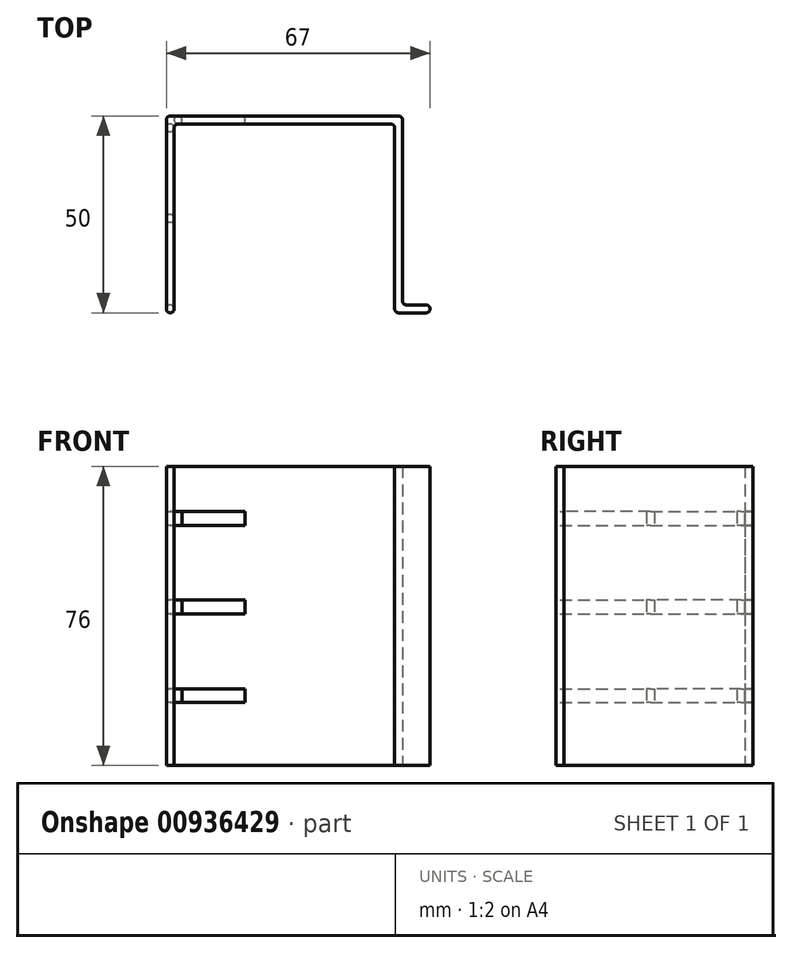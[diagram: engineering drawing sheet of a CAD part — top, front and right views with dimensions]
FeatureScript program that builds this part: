
annotation { "Feature Type Name" : "Feature", "Feature Type Description" : "" }
export const myFeature = defineFeature(function(context is Context, id is Id, definition is map)
    precondition{}
    {
        {
            var Q0;
            Q0=qCreatedBy(makeId("Top.planeOp"),FACE);
            var sketch = newSketch(context, id + "F0", { "sketchPlane" : qUnion([Q0])});
            skLineSegment(sketch, "E0", {"start": v(0, 1) * mm, "end": v(0, 47) * mm});
            skLineSegment(sketch, "E1", {"start": v(1, 48) * mm, "end": v(55, 48) * mm});
            skLineSegment(sketch, "E2", {"start": v(56, 47) * mm, "end": v(56, 1) * mm});
            skLineSegment(sketch, "E3", {"start": v(57, 0) * mm, "end": v(64, 0) * mm});
            skLineSegment(sketch, "E4.0", {"start": v(59, 2) * mm, "end": v(64, 2) * mm});
            skLineSegment(sketch, "E4.1", {"start": v(58, 49) * mm, "end": v(58, 3) * mm});
            skLineSegment(sketch, "E4.2", {"start": v(-1, 50) * mm, "end": v(57, 50) * mm});
            skLineSegment(sketch, "E4.3", {"start": v(-2, 1) * mm, "end": v(-2, 49) * mm});
            skLineSegment(sketch, "E5", {"start": v(65, 1) * mm, "end": v(65, 1) * mm});
            skLineSegment(sketch, "E6", {"start": v(-1, 0) * mm, "end": v(-1, 0) * mm});
            skPoint(sketch, "E7.visualSharp", {"position": v(0, 48) * mm});
            skArc(sketch, "E7.filletArc", {"start": v(1, 48) * mm, "mid": v(0.3, 47.7) * mm, "end": v(0, 47) * mm});
            skPoint(sketch, "E8.visualSharp", {"position": v(-2, 50) * mm});
            skArc(sketch, "E8.filletArc", {"start": v(-1, 50) * mm, "mid": v(-1.7, 49.7) * mm, "end": v(-2, 49) * mm});
            skPoint(sketch, "E9.visualSharp", {"position": v(58, 50) * mm});
            skArc(sketch, "E9.filletArc", {"start": v(58, 49) * mm, "mid": v(57.7, 49.7) * mm, "end": v(57, 50) * mm});
            skPoint(sketch, "E10.visualSharp", {"position": v(56, 48) * mm});
            skArc(sketch, "E10.filletArc", {"start": v(56, 47) * mm, "mid": v(55.7, 47.7) * mm, "end": v(55, 48) * mm});
            skPoint(sketch, "E11.visualSharp", {"position": v(58, 2) * mm});
            skArc(sketch, "E11.filletArc", {"start": v(58, 3) * mm, "mid": v(58.3, 2.3) * mm, "end": v(59, 2) * mm});
            skPoint(sketch, "E12.visualSharp", {"position": v(56, 0) * mm});
            skArc(sketch, "E12.filletArc", {"start": v(56, 1) * mm, "mid": v(56.3, 0.3) * mm, "end": v(57, 0) * mm});
            skPoint(sketch, "E13.visualSharp", {"position": v(65, 2) * mm});
            skArc(sketch, "E13.filletArc", {"start": v(65, 1) * mm, "mid": v(64.7, 1.7) * mm, "end": v(64, 2) * mm});
            skPoint(sketch, "E14.visualSharp", {"position": v(65, 0) * mm});
            skArc(sketch, "E14.filletArc", {"start": v(64, 0) * mm, "mid": v(64.7, 0.3) * mm, "end": v(65, 1) * mm});
            skPoint(sketch, "E15.visualSharp", {"position": v(-2, 0) * mm});
            skArc(sketch, "E15.filletArc", {"start": v(-2, 1) * mm, "mid": v(-1.7, 0.3) * mm, "end": v(-1, 0) * mm});
            skPoint(sketch, "E16.visualSharp", {"position": v(0, 0) * mm});
            skArc(sketch, "E16.filletArc", {"start": v(-1, 0) * mm, "mid": v(-0.3, 0.3) * mm, "end": v(0, 1) * mm});
            skSolve(sketch);
        }
        {
            var Q0;
            Q0=makeQuery(id+"F0.imprint","IMPRINT",FACE,{"disambiguationData":[TD([[makeQuery(id+"F0.imprint","IMPRINT",EDGE,{"derivedFrom":sQuery(id+"F0.wireOp",EDGE,"E0")}),1.0]])]});
            extrude(context, id + "F1", {"entities" : qUnion([Q0]), "depth" : 76 * mm, "offsetDistance" : 25 * mm});
        }
        {
            var Q0;
            Q0=makeQuery(id+"F1.opExtrude","SWEPT_FACE",FACE,{"disambiguationData":[OSD([sQuery(id+"F0.wireOp",EDGE,"E4.2")])]});
            var sketch = newSketch(context, id + "F2", { "sketchPlane" : qUnion([Q0])});
            skLineSegment(sketch, "E17", {"start": v(2, 16) * mm, "end": v(-18, 16) * mm});
            skLineSegment(sketch, "E18", {"start": v(-18, 16) * mm, "end": v(-18, 19.5) * mm});
            skLineSegment(sketch, "E19", {"start": v(-18, 19.5) * mm, "end": v(2, 19.5) * mm});
            skLineSegment(sketch, "E20.0", {"start": v(2, 76) * mm, "end": v(2, 0) * mm});
            skLineSegment(sketch, "E21", {"start": v(2, 19.5) * mm, "end": v(2, 16) * mm});
            skLineSegment(sketch, "E22.0.1.0", {"start": v(-18, 42) * mm, "end": v(2, 42) * mm});
            skLineSegment(sketch, "E22.0.1.1", {"start": v(2, 42) * mm, "end": v(2, 38.5) * mm});
            skLineSegment(sketch, "E22.0.1.2", {"start": v(2, 38.5) * mm, "end": v(-18, 38.5) * mm});
            skLineSegment(sketch, "E22.0.1.3", {"start": v(-18, 38.5) * mm, "end": v(-18, 42) * mm});
            skLineSegment(sketch, "E22.0.2.0", {"start": v(-18, 64.5) * mm, "end": v(2, 64.5) * mm});
            skLineSegment(sketch, "E22.0.2.1", {"start": v(2, 64.5) * mm, "end": v(2, 61) * mm});
            skLineSegment(sketch, "E22.0.2.2", {"start": v(2, 61) * mm, "end": v(-18, 61) * mm});
            skLineSegment(sketch, "E22.0.2.3", {"start": v(-18, 61) * mm, "end": v(-18, 64.5) * mm});
            skLineSegment(sketch, "E22.direction1", {"start": v(-18, 16) * mm, "end": v(7, 16) * mm, "construction": true});
            skLineSegment(sketch, "E22.direction2", {"start": v(-18, 16) * mm, "end": v(-18, 38.5) * mm, "construction": true});
            skSolve(sketch);
        }
        {
            var Q0;
            {var subQ0=sQuery(id+"F2.wireOp",EDGE,"E18");var subQ1=sQuery(id+"F2.wireOp",EDGE,"E17");var subQ7=sQuery(id+"F2.wireOp",EDGE,"E20.0");var subQ8=makeQuery(id+"F2.imprint","INTERSECT",VERTEX,{"derivedFrom":[subQ1,subQ7]});Q0=qUnion([makeQuery(id+"F2.imprint","IMPRINT",FACE,{"disambiguationData":[TD([[makeQuery(id+"F2.imprint","IMPRINT",EDGE,{"disambiguationData":[TD([[subQ8,1.0]])],"derivedFrom":subQ7}),-1.0]])]}),makeQuery(id+"F2.imprint","IMPRINT",FACE,{"disambiguationData":[TD([[makeQuery(id+"F2.imprint","IMPRINT",EDGE,{"derivedFrom":subQ0}),-1.0]])]})]);}
            var Q1;
            Q1=makeQuery(id+"F2.imprint","IMPRINT",FACE,{"disambiguationData":[TD([[makeQuery(id+"F2.imprint","IMPRINT",EDGE,{"derivedFrom":sQuery(id+"F2.wireOp",EDGE,"e2ad7010-09eb-4918-bae3-de0be9d5e85c.0.1.0")}),-1.0]])]});
            var Q2;
            Q2=makeQuery(id+"F2.imprint","IMPRINT",FACE,{"disambiguationData":[TD([[makeQuery(id+"F2.imprint","IMPRINT",EDGE,{"derivedFrom":sQuery(id+"F2.wireOp",EDGE,"e2ad7010-09eb-4918-bae3-de0be9d5e85c.0.2.0")}),-1.0]])]});
            var Q3;
            {var subQ0=sQuery(id+"F2.wireOp",EDGE,"E22.0.1.3");Q3=makeQuery(id+"F2.imprint","IMPRINT",FACE,{"disambiguationData":[TD([[makeQuery(id+"F2.imprint","IMPRINT",EDGE,{"derivedFrom":subQ0}),-1.0]])]});}
            var Q4;
            {var subQ0=sQuery(id+"F2.wireOp",EDGE,"E22.0.2.3");Q4=makeQuery(id+"F2.imprint","IMPRINT",FACE,{"disambiguationData":[TD([[makeQuery(id+"F2.imprint","IMPRINT",EDGE,{"derivedFrom":subQ0}),-1.0]])]});}
            var Q5;
            {var subQ0=sQuery(id+"F2.wireOp",EDGE,"E22.0.1.0");var subQ1=sQuery(id+"F2.wireOp",EDGE,"E20.0");var subQ2=makeQuery(id+"F2.imprint","INTERSECT",VERTEX,{"derivedFrom":[subQ1,subQ0]});Q5=makeQuery(id+"F2.imprint","IMPRINT",FACE,{"disambiguationData":[TD([[makeQuery(id+"F2.imprint","IMPRINT",EDGE,{"disambiguationData":[TD([[subQ2,-1.0]])],"derivedFrom":subQ1}),-1.0]])]});}
            var Q6;
            {var subQ0=sQuery(id+"F2.wireOp",EDGE,"E22.0.2.2");var subQ1=sQuery(id+"F2.wireOp",EDGE,"E20.0");var subQ2=makeQuery(id+"F2.imprint","INTERSECT",VERTEX,{"derivedFrom":[subQ1,subQ0]});Q6=makeQuery(id+"F2.imprint","IMPRINT",FACE,{"disambiguationData":[TD([[makeQuery(id+"F2.imprint","IMPRINT",EDGE,{"disambiguationData":[TD([[subQ2,1.0]])],"derivedFrom":subQ1}),-1.0]])]});}
            extrude(context, id + "F3", {"entities" : qUnion([Q0, Q1, Q2, Q3, Q4, Q5, Q6]), "operationType" : NewBodyOperationType.REMOVE, "endBound" : BoundingType.THROUGH_ALL, "oppositeDirection" : true, "depth" : 25 * mm, "offsetDistance" : 25 * mm});
        }
        {
            var Q0;
            Q0=makeQuery(id+"F3.boolean.opBoolean","COPY",FACE,{"derivedFrom":makeQuery(id+"F3.opExtrude","SWEPT_FACE",FACE,{"disambiguationData":[OSD([sQuery(id+"F2.wireOp",EDGE,"E17")])]})});
            var sketch = newSketch(context, id + "F4", { "sketchPlane" : qUnion([Q0])});
            skLineSegment(sketch, "E23.0", {"start": v(-2, 1) * mm, "end": v(-2, 49) * mm});
            skPoint(sketch, "E24.0", {"position": v(-1.7, 49.7) * mm});
            skLineSegment(sketch, "E25.0", {"start": v(-1, 50) * mm, "end": v(18, 50) * mm});
            skLineSegment(sketch, "E26.0", {"start": v(1, 48) * mm, "end": v(18, 48) * mm});
            skArc(sketch, "E27.0", {"start": v(1, 48) * mm, "mid": v(0.3, 47.7) * mm, "end": v(0, 47) * mm});
            skLineSegment(sketch, "E28.0", {"start": v(0, 1) * mm, "end": v(0, 47) * mm});
            skLineSegment(sketch, "E29.0", {"start": v(18, 48) * mm, "end": v(18, 50) * mm});
            skArc(sketch, "E30.0", {"start": v(-2, 1) * mm, "mid": v(-1, 0) * mm, "end": v(0, 1) * mm});
            skArc(sketch, "E31.0", {"start": v(-1, 50) * mm, "mid": v(-1.7, 49.7) * mm, "end": v(-2, 49) * mm});
            skCircle(sketch, "E32", {"center": v(-1, 1) * mm, "radius": 1 * mm});
            skCircle(sketch, "E33", {"center": v(-1, 47) * mm, "radius": 1 * mm});
            skCircle(sketch, "E34", {"center": v(-1, 24) * mm, "radius": 1 * mm});
            skLineSegment(sketch, "E35", {"start": v(0, 47) * mm, "end": v(-2, 47) * mm, "construction": true});
            skLineSegment(sketch, "E36", {"start": v(-1, 47) * mm, "end": v(-1, 1) * mm, "construction": true});
            skLineSegment(sketch, "E37", {"start": v(1, 48) * mm, "end": v(1, 50) * mm, "construction": true});
            skCircle(sketch, "E38", {"center": v(1, 49) * mm, "radius": 1 * mm});
            skSolve(sketch);
        }
        {
            var Q0;
            Q0=makeQuery(id+"F4.imprint","IMPRINT",FACE,{"disambiguationData":[TD([[makeQuery(id+"F4.imprint","IMPRINT",EDGE,{"derivedFrom":sQuery(id+"F4.wireOp",EDGE,"E33")}),1.0]])]});
            var Q1;
            Q1=makeQuery(id+"F4.imprint","IMPRINT",FACE,{"disambiguationData":[TD([[makeQuery(id+"F4.imprint","IMPRINT",EDGE,{"derivedFrom":sQuery(id+"F4.wireOp",EDGE,"E34")}),1.0]])]});
            var Q2;
            Q2=makeQuery(id+"F4.imprint","IMPRINT",FACE,{"disambiguationData":[TD([[makeQuery(id+"F4.imprint","IMPRINT",EDGE,{"derivedFrom":sQuery(id+"F4.wireOp",EDGE,"E32")}),1.0]])]});
            var Q3;
            {var subQ0=sQuery(id+"F4.wireOp",EDGE,"E38");var subQ2=makeQuery(id+"F4.imprint","INTERSECT",VERTEX,{"derivedFrom":[sQuery(id+"F4.wireOp",EDGE,"E25.0"),subQ0]});Q3=makeQuery(id+"F4.imprint","IMPRINT",FACE,{"disambiguationData":[TD([[makeQuery(id+"F4.imprint","IMPRINT",EDGE,{"disambiguationData":[TD([[subQ2,-1.0]])],"derivedFrom":subQ0}),1.0]])]});}
            var Q4;
            Q4=sQuery(id+"F4.wireOp",EDGE,"E33");
            var Q5;
            Q5=sQuery(id+"F4.wireOp",EDGE,"E34");
            var Q6;
            Q6=sQuery(id+"F4.wireOp",EDGE,"E32");
            var Q7;
            Q7=makeQuery(id+"F3.boolean.opBoolean","COPY",FACE,{"derivedFrom":makeQuery(id+"F3.opExtrude","SWEPT_FACE",FACE,{"disambiguationData":[OSD([sQuery(id+"F2.wireOp",EDGE,"E22.0.2.0")])]})});
            extrude(context, id + "F5", {"entities" : qUnion([Q0, Q1, Q2, Q3]), "operationType" : NewBodyOperationType.ADD, "surfaceEntities" : qUnion([Q4, Q5, Q6]), "endBound" : BoundingType.UP_TO_SURFACE, "depth" : 25 * mm, "endBoundEntityFace" : qUnion([Q7]), "offsetDistance" : 25 * mm});
        }
    });
